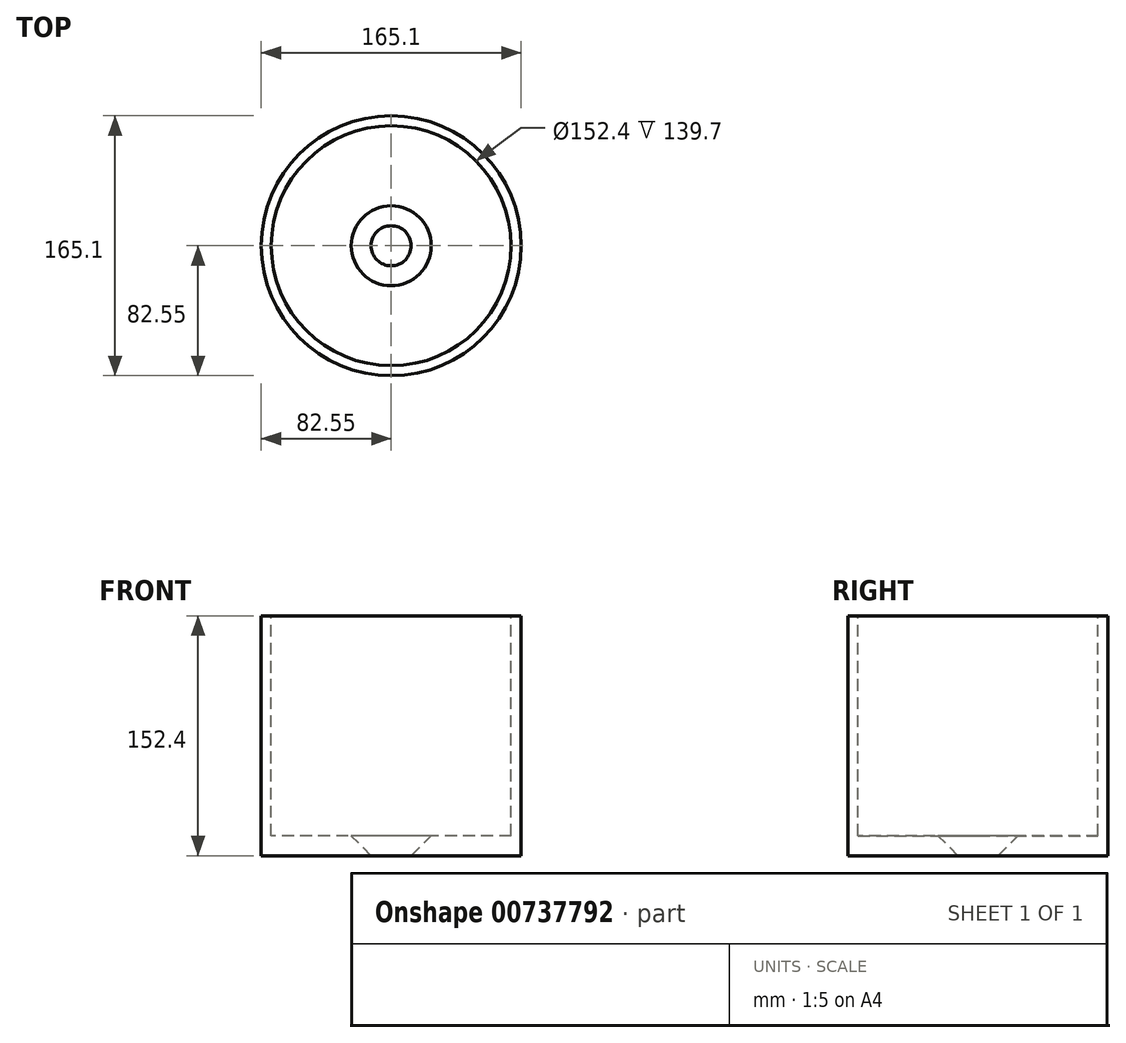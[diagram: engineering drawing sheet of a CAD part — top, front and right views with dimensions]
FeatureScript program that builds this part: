
annotation { "Feature Type Name" : "Feature", "Feature Type Description" : "" }
export const myFeature = defineFeature(function(context is Context, id is Id, definition is map)
    precondition{}
    {
        {
            var Q0;
            Q0=qCreatedBy(makeId("Front.planeOp"),FACE);
            var sketch = newSketch(context, id + "F0", { "sketchPlane" : qUnion([Q0])});
            skLineSegment(sketch, "E0", {"start": v(12.7, 0) * mm, "end": v(25.4, 12.7) * mm});
            skLineSegment(sketch, "E1", {"start": v(25.4, 12.7) * mm, "end": v(76.2, 12.7) * mm});
            skLineSegment(sketch, "E2", {"start": v(76.2, 12.7) * mm, "end": v(76.2, 152.4) * mm});
            skLineSegment(sketch, "E3", {"start": v(76.2, 152.4) * mm, "end": v(82.55, 152.4) * mm});
            skLineSegment(sketch, "E4", {"start": v(82.55, 152.4) * mm, "end": v(82.55, 0) * mm});
            skLineSegment(sketch, "E5", {"start": v(82.55, 0) * mm, "end": v(12.7, 0) * mm});
            skSolve(sketch);
        }
        {
            var Q0;
            Q0=qCreatedBy(makeId("Front.planeOp"),FACE);
            var sketch = newSketch(context, id + "F1", { "sketchPlane" : qUnion([Q0])});
            skLineSegment(sketch, "E6", {"start": v(0, 35.74) * mm, "end": v(0, -26.32) * mm});
            skSolve(sketch);
        }
        {
            var Q0;
            Q0 = qSketchRegion(id + "F0", true);
            var Q1;
            Q1=sQuery(id+"F1.wireOp",EDGE,"E6");
            revolve(context, id + "F2", {"surfaceOperationType" : NewSurfaceOperationType.NEW, "entities" : qUnion([Q0]), "axis" : qUnion([Q1]), "revolveType" : RevolveType.FULL});
        }
    });
